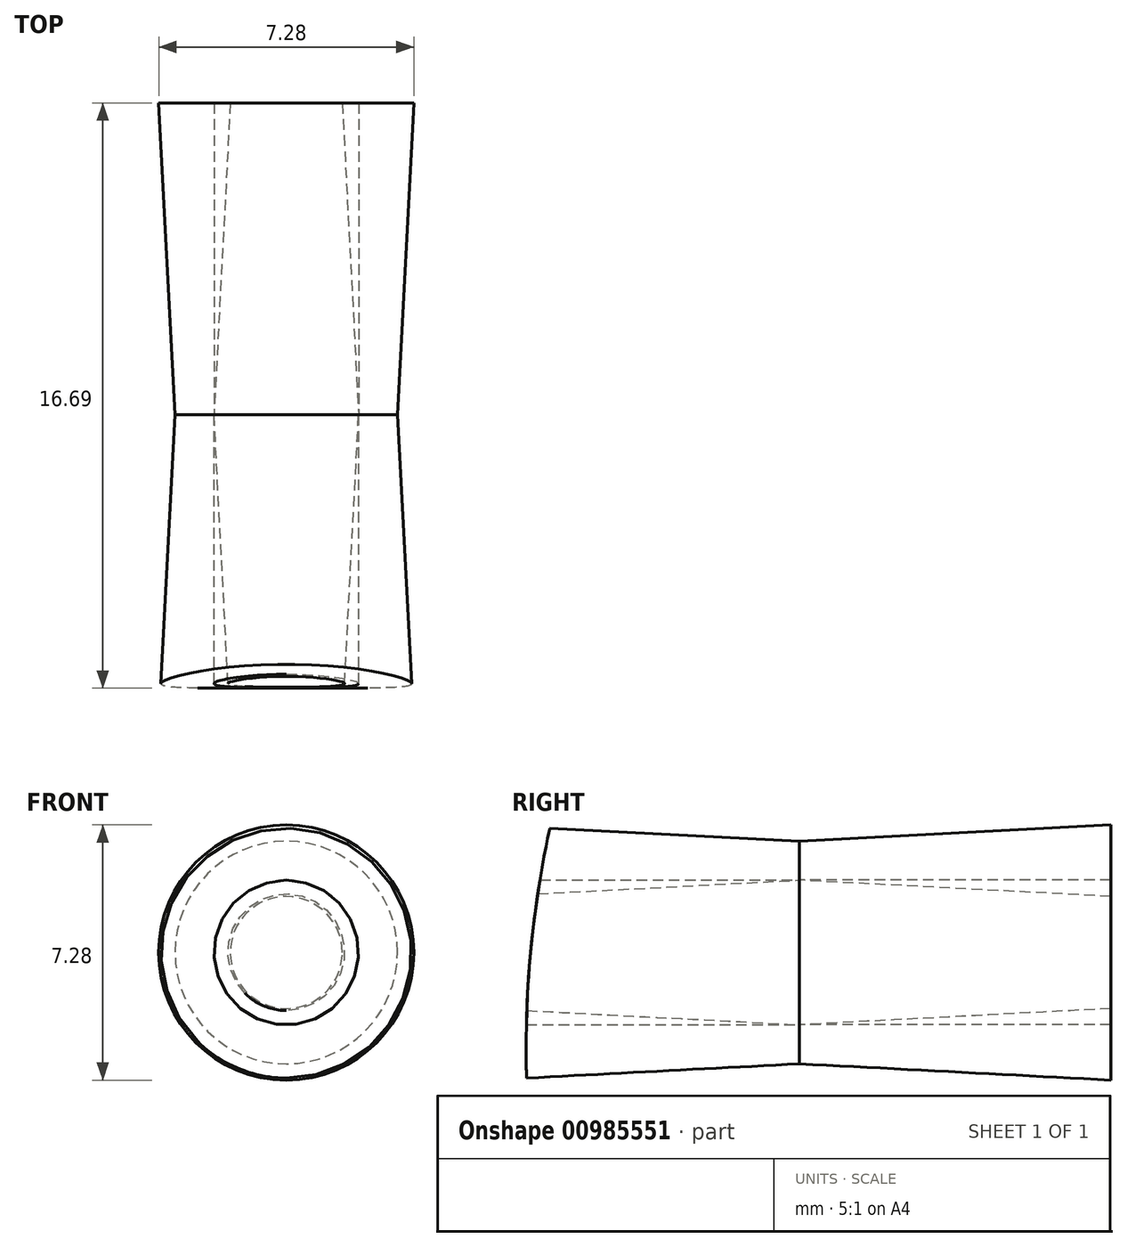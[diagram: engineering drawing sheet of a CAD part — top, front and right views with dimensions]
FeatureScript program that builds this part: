
annotation { "Feature Type Name" : "Feature", "Feature Type Description" : "" }
export const myFeature = defineFeature(function(context is Context, id is Id, definition is map)
    precondition{}
    {
        {
            var Q0;
            Q0=qCreatedBy(makeId("Front.planeOp"),FACE);
            var sketch = newSketch(context, id + "F0", { "sketchPlane" : qUnion([Q0])});
            skFitSpline(sketch, "E0", {"points": [v(-150.67, 0) * mm, v(-115.86, 15.93) * mm, v(40.24, 26.94) * mm, v(160.89, 14.5) * mm], "startDerivative": vector(125.16, 81.4) * mm, "endDerivative": vector(239.4, -48.85) * mm});
            skArc(sketch, "E1", {"start": v(-150.67, 0) * mm, "mid": v(-52.87, -29.1) * mm, "end": v(48.74, -38.24) * mm});
            skFitSpline(sketch, "E2", {"points": [v(52.53, -38.19) * mm, v(61, -7.18) * mm, v(74.1, 0) * mm, v(104.17, -6.4) * mm, v(162.23, 0) * mm], "startDerivative": vector(7.94, 140.64) * mm, "endDerivative": vector(188.15, 36.2) * mm});
            skArc(sketch, "E3", {"start": v(164.3, 1.35) * mm, "mid": v(166.6, 8.79) * mm, "end": v(161.22, 14.42) * mm});
            skArc(sketch, "E4.filletArc", {"start": v(48.74, -38.24) * mm, "mid": v(51.5, -37.15) * mm, "end": v(52.81, -34.5) * mm});
            skLineSegment(sketch, "E5", {"start": v(52.53, -38.19) * mm, "end": v(52.53, -35.65) * mm});
            skLineSegment(sketch, "E6", {"start": v(-150.67, 0) * mm, "end": v(52.53, 0) * mm, "construction": true});
            skPoint(sketch, "E6.endSnap0", {"position": v(52.53, -5.82) * mm});
            skLineSegment(sketch, "E7", {"start": v(167.4, -55.76) * mm, "end": v(167.4, 53.93) * mm, "construction": true});
            skPoint(sketch, "E8.orphan", {"position": v(-184.2, 23.18) * mm});
            skPoint(sketch, "E9.orphan", {"position": v(52.53, -52.89) * mm});
            skPoint(sketch, "E10.start.orphan", {"position": v(-184.2, 0) * mm});
            skLineSegment(sketch, "E11", {"start": v(52.53, 38.01) * mm, "end": v(-150.67, 76.2) * mm, "construction": true});
            skLineSegment(sketch, "E12", {"start": v(164.2, 58.28) * mm, "end": v(199.92, -20.95) * mm, "construction": true});
            skLineSegment(sketch, "E13", {"start": v(51.85, 67.77) * mm, "end": v(-151.66, 35.38) * mm, "construction": true});
            skPoint(sketch, "E14.end.orphan", {"position": v(52.53, 63.54) * mm});
            skPoint(sketch, "E15", {"position": v(76.45, 12.11) * mm});
            skPoint(sketch, "E16", {"position": v(148.54, 7.43) * mm});
            skPoint(sketch, "E17", {"position": v(112.5, 9.77) * mm});
            skLineSegment(sketch, "E18", {"start": v(40.24, 26.94) * mm, "end": v(58.3, -11.96) * mm});
            skArc(sketch, "E19.filletArc", {"start": v(161.22, 14.42) * mm, "mid": v(160.98, 14.48) * mm, "end": v(160.75, 14.53) * mm});
            skArc(sketch, "E20.filletArc", {"start": v(161.22, -0.2) * mm, "mid": v(162.86, 0.36) * mm, "end": v(164.3, 1.35) * mm});
            skPoint(sketch, "E21", {"position": v(63.5, 26.03) * mm});
            skPoint(sketch, "E22", {"position": v(66.39, -2) * mm});
            skArc(sketch, "E23", {"start": v(61.43, 24.87) * mm, "mid": v(54.86, 11.5) * mm, "end": v(63.17, -0.87) * mm});
            skArc(sketch, "E24.filletArc", {"start": v(65.3, 25.94) * mm, "mid": v(63.28, 25.72) * mm, "end": v(61.43, 24.87) * mm});
            skArc(sketch, "E25.filletArc", {"start": v(63.17, -0.87) * mm, "mid": v(65.72, -1.5) * mm, "end": v(68.31, -1.06) * mm});
            skCircle(sketch, "E26", {"center": v(76.45, 12.11) * mm, "radius": 3.18 * mm});
            skCircle(sketch, "E27", {"center": v(76.45, 12.11) * mm, "radius": 2.06 * mm});
            skSolve(sketch);
        }
        {
            var Q0;
            Q0=qCreatedBy(makeId("Right.planeOp"),FACE);
            var sketch = newSketch(context, id + "F1", { "sketchPlane" : qUnion([Q0])});
            skArc(sketch, "E28", {"start": v(-2.54, 26.16) * mm, "mid": v(-7.8, 9.61) * mm, "end": v(-2.8, -7.01) * mm});
            skLineSegment(sketch, "E29", {"start": v(-2.8, -7.01) * mm, "end": v(-10.98, -7.01) * mm});
            skLineSegment(sketch, "E30", {"start": v(-10.98, -7.01) * mm, "end": v(-10.98, 26.16) * mm});
            skLineSegment(sketch, "E31", {"start": v(-10.98, 26.16) * mm, "end": v(-2.54, 26.16) * mm});
            skLineSegment(sketch, "E32", {"start": v(0, -14.87) * mm, "end": v(0, 34.35) * mm, "construction": true});
            skArc(sketch, "E33.MirrorCS", {"start": v(2.54, 26.16) * mm, "mid": v(7.8, 9.61) * mm, "end": v(2.8, -7.01) * mm});
            skLineSegment(sketch, "E34.MirrorCS", {"start": v(10.98, -7.01) * mm, "end": v(10.98, 26.16) * mm});
            skLineSegment(sketch, "E35.MirrorCS", {"start": v(2.8, -7.01) * mm, "end": v(10.98, -7.01) * mm});
            skLineSegment(sketch, "E36.MirrorCS", {"start": v(10.98, 26.16) * mm, "end": v(2.54, 26.16) * mm});
            skSolve(sketch);
        }
        {
            var Q0;
            Q0=makeQuery(id+"F0.imprint","IMPRINT",FACE,{"disambiguationData":[TD([[makeQuery(id+"F0.imprint","IMPRINT",EDGE,{"derivedFrom":sQuery(id+"F0.wireOp",EDGE,"E27")}),1.0]])]});
            extrude(context, id + "F2", {"entities" : qUnion([Q0]), "depth" : 8.9 * mm, "offsetDistance" : 25.4 * mm});
        }
        {
            var Q0;
            Q0=makeQuery(id+"F0.imprint","IMPRINT",FACE,{"disambiguationData":[TD([[makeQuery(id+"F0.imprint","IMPRINT",EDGE,{"derivedFrom":sQuery(id+"F0.wireOp",EDGE,"E26")}),1.0]])]});
            extrude(context, id + "F3", {"entities" : qUnion([Q0]), "depth" : 8.9 * mm, "offsetDistance" : 25.4 * mm, "hasDraft" : true, "draftAngle" : 3 * degree});
        }
        {
            var Q0;
            Q0=makeQuery(id+"F2.opExtrude","SWEPT_BODY",BODY,{"disambiguationData":[OSD([sQuery(id+"F0.wireOp",EDGE,"E27")])]});
            var Q1;
            Q1=makeQuery(id+"F3.opExtrude","SWEPT_BODY",BODY,{"disambiguationData":[OSD([sQuery(id+"F0.wireOp",EDGE,"E26"),sQuery(id+"F0.wireOp",EDGE,"E27")])]});
            var Q2;
            Q2=qCreatedBy(makeId("Front.planeOp"),FACE);
            mirror(context, id + "F4", {"entities" : qUnion([Q0, Q1]), "mirrorPlane" : qUnion([Q2])});
        }
        {
            var Q0;
            Q0=makeQuery(id+"F1.imprint","IMPRINT",FACE,{"disambiguationData":[TD([[makeQuery(id+"F1.imprint","IMPRINT",EDGE,{"derivedFrom":sQuery(id+"F1.wireOp",EDGE,"E28")}),-1.0]])]});
            var Q1;
            Q1=makeQuery(id+"F1.imprint","IMPRINT",FACE,{"disambiguationData":[TD([[makeQuery(id+"F1.imprint","IMPRINT",EDGE,{"derivedFrom":sQuery(id+"F1.wireOp",EDGE,"E33.MirrorCS")}),1.0]])]});
            extrude(context, id + "F5", {"entities" : qUnion([Q0, Q1]), "operationType" : NewBodyOperationType.REMOVE, "endBound" : BoundingType.THROUGH_ALL, "depth" : 127 * mm, "offsetDistance" : 25.4 * mm});
        }
    });
